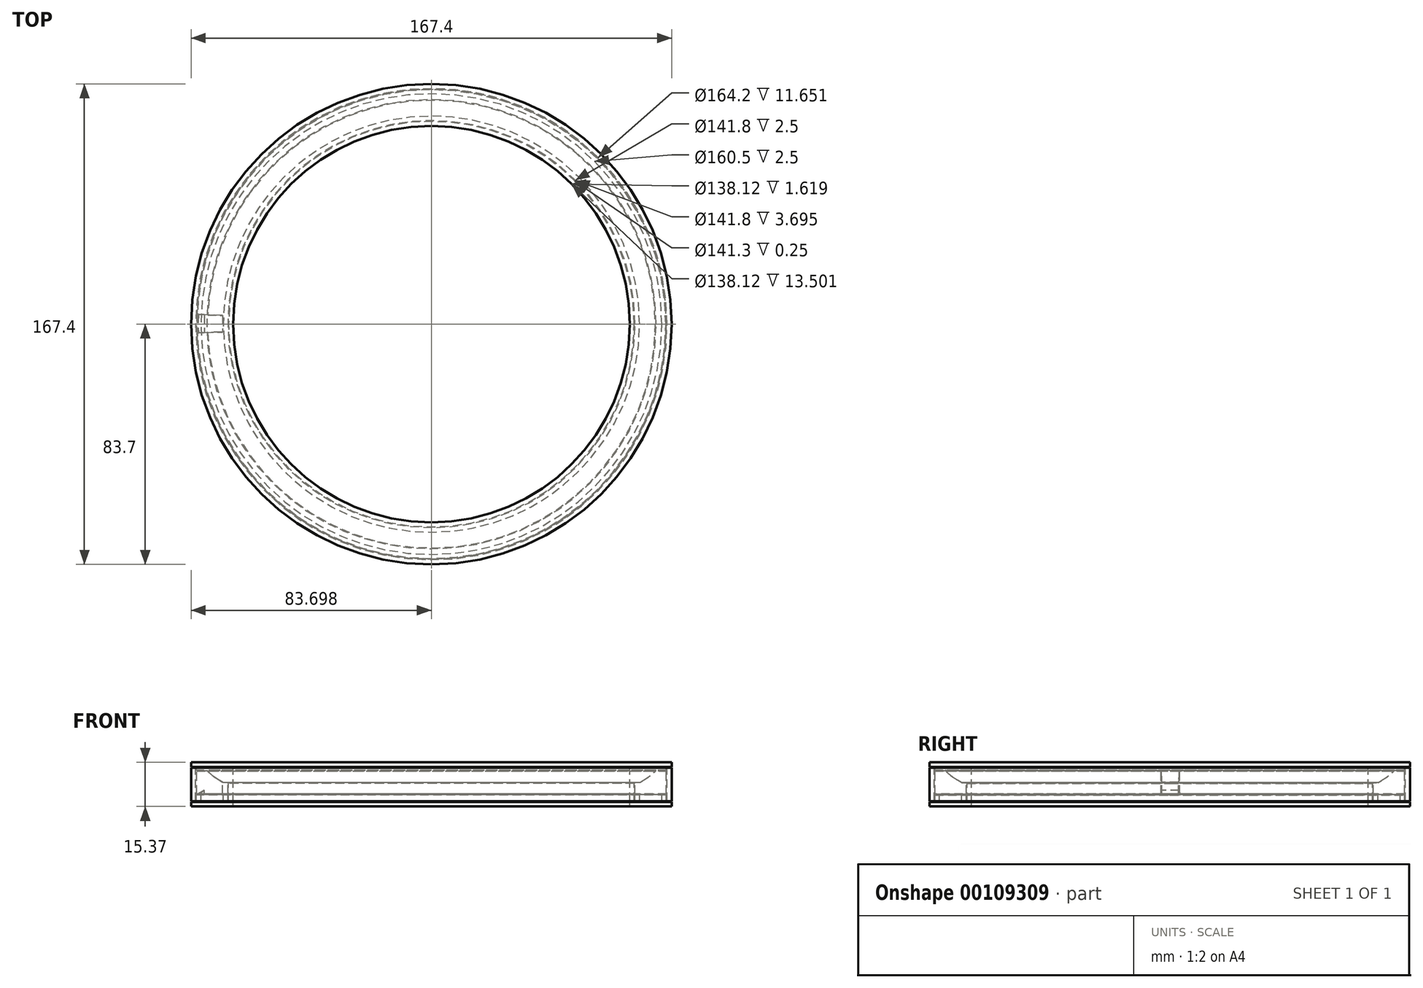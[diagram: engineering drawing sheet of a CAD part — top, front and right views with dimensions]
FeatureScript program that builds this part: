
annotation { "Feature Type Name" : "Feature", "Feature Type Description" : "" }
export const myFeature = defineFeature(function(context is Context, id is Id, definition is map)
    precondition{}
    {
        {
            var Q0;
            Q0=qCreatedBy(makeId("Front.planeOp"),FACE);
            var sketch = newSketch(context, id + "F0", { "sketchPlane" : qUnion([Q0])});
            skLineSegment(sketch, "E0", {"start": v(49.07, 29.5) * mm, "end": v(49.07, -21.25) * mm, "construction": true});
            skLineSegment(sketch, "E1", {"start": v(-23.43, 29.5) * mm, "end": v(-23.43, -21.25) * mm, "construction": true});
            skLineSegment(sketch, "E2", {"start": v(-30.18, 1.62) * mm, "end": v(-23.68, 1.62) * mm, "construction": true});
            skLineSegment(sketch, "E3", {"start": v(-23.68, 1.62) * mm, "end": v(-23.68, 4.12) * mm, "construction": true});
            skLineSegment(sketch, "E4", {"start": v(-23.68, 4.12) * mm, "end": v(-30.18, 4.12) * mm, "construction": true});
            skLineSegment(sketch, "E5", {"start": v(-30.18, 4.12) * mm, "end": v(-30.18, 1.62) * mm, "construction": true});
            skLineSegment(sketch, "E6", {"start": v(-29.18, 4.12) * mm, "end": v(-29.18, 4.92) * mm, "construction": true});
            skLineSegment(sketch, "E7", {"start": v(-29.18, 4.92) * mm, "end": v(-24.68, 4.92) * mm, "construction": true});
            skLineSegment(sketch, "E8", {"start": v(-24.68, 4.92) * mm, "end": v(-24.68, 4.12) * mm, "construction": true});
            skLineSegment(sketch, "E9", {"start": v(-35.93, 29.5) * mm, "end": v(-35.93, -21.25) * mm, "construction": true});
            skLineSegment(sketch, "E10", {"start": v(-31.18, 1.62) * mm, "end": v(-23.43, 1.62) * mm});
            skLineSegment(sketch, "E11", {"start": v(-31.18, 1.62) * mm, "end": v(-31.18, 4.12) * mm});
            skLineSegment(sketch, "E12", {"start": v(-34.74, 0.02) * mm, "end": v(-21.83, 0.02) * mm});
            skLineSegment(sketch, "E13", {"start": v(-23.43, 1.62) * mm, "end": v(-23.43, 3.24) * mm});
            skLineSegment(sketch, "E14", {"start": v(-23.43, 4.12) * mm, "end": v(-21.83, 4.12) * mm});
            skLineSegment(sketch, "E15", {"start": v(-21.83, 4.12) * mm, "end": v(-21.83, 0.02) * mm});
            skLineSegment(sketch, "E16", {"start": v(-24.68, 4.92) * mm, "end": v(-24.68, 12.8) * mm, "construction": true});
            skLineSegment(sketch, "E17", {"start": v(-29.18, 4.92) * mm, "end": v(-29.18, 12.8) * mm, "construction": true});
            skLineSegment(sketch, "E18", {"start": v(-82.01, -1.66) * mm, "end": v(-82.01, 10.37) * mm, "construction": true});
            skLineSegment(sketch, "E19", {"start": v(-23.43, 4.12) * mm, "end": v(-23.43, 1.62) * mm});
            skLineSegment(sketch, "E20", {"start": v(-72.42, 0.02) * mm, "end": v(839.7, 0.02) * mm, "construction": true});
            skLineSegment(sketch, "E21", {"start": v(-21.58, 1.87) * mm, "end": v(-21.58, 20.5) * mm});
            skLineSegment(sketch, "E22", {"start": v(-20, 1.87) * mm, "end": v(-20, 15.37) * mm});
            skLineSegment(sketch, "E23", {"start": v(-20, 15.37) * mm, "end": v(-34.63, 15.37) * mm});
            skLineSegment(sketch, "E24", {"start": v(-34.63, 13.52) * mm, "end": v(-33.03, 13.52) * mm});
            skLineSegment(sketch, "E25", {"start": v(-33.03, 13.52) * mm, "end": v(-33.03, 1.87) * mm});
            skLineSegment(sketch, "E26", {"start": v(-33.03, 1.87) * mm, "end": v(-34.63, 1.87) * mm});
            skLineSegment(sketch, "E27", {"start": v(-34.63, 1.87) * mm, "end": v(-34.63, 13.52) * mm});
            skLineSegment(sketch, "E28", {"start": v(-34.63, 0.02) * mm, "end": v(-34.74, 0.02) * mm});
            skLineSegment(sketch, "E29", {"start": v(-34.63, 0.02) * mm, "end": v(-34.63, 1.62) * mm});
            skLineSegment(sketch, "E30", {"start": v(-34.63, 1.62) * mm, "end": v(-32.78, 1.62) * mm});
            skLineSegment(sketch, "E31", {"start": v(-34.63, 15.37) * mm, "end": v(-34.63, 13.77) * mm});
            skLineSegment(sketch, "E32", {"start": v(-34.63, 13.77) * mm, "end": v(-32.78, 13.77) * mm});
            skLineSegment(sketch, "E33", {"start": v(-36.84, 4.37) * mm, "end": v(-22.3, 4.37) * mm, "construction": true});
            skLineSegment(sketch, "E34", {"start": v(-32.78, 1.62) * mm, "end": v(-32.78, 2.82) * mm});
            skLineSegment(sketch, "E35", {"start": v(-32.78, 13.77) * mm, "end": v(-32.78, 12.57) * mm});
            skLineSegment(sketch, "E36", {"start": v(-32.78, 12.57) * mm, "end": v(-28.4, 12.57) * mm});
            skLineSegment(sketch, "E37", {"start": v(-23.43, 8.31) * mm, "end": v(-21.58, 8.31) * mm});
            skLineSegment(sketch, "E38", {"start": v(-21.83, 4.37) * mm, "end": v(-31.4, 4.37) * mm});
            skLineSegment(sketch, "E39", {"start": v(-31.4, 4.37) * mm, "end": v(-32.78, 4.37) * mm});
            skLineSegment(sketch, "E40.0", {"start": v(-32.78, 12.32) * mm, "end": v(-28.4, 12.32) * mm});
            skLineSegment(sketch, "E41", {"start": v(-32.78, 12.32) * mm, "end": v(-32.78, 4.37) * mm});
            skLineSegment(sketch, "E42", {"start": v(-23.43, 8.31) * mm, "end": v(-24.68, 9.04) * mm});
            skLineSegment(sketch, "E43", {"start": v(-22.53, 10.28) * mm, "end": v(-40.3, 0.02) * mm, "construction": true});
            skArc(sketch, "E44", {"start": v(-24.68, 9.04) * mm, "mid": v(-27.06, 10.64) * mm, "end": v(-29.18, 12.57) * mm});
            skLineSegment(sketch, "E45", {"start": v(-29.18, 12.57) * mm, "end": v(-28.4, 12.57) * mm});
            skArc(sketch, "E46.0", {"start": v(-24.78, 8.8) * mm, "mid": v(-27.19, 10.43) * mm, "end": v(-29.34, 12.37) * mm});
            skLineSegment(sketch, "E47", {"start": v(-29.29, 12.32) * mm, "end": v(-28.4, 12.32) * mm});
            skLineSegment(sketch, "E48.0", {"start": v(-23.5, 8.06) * mm, "end": v(-24.8, 8.81) * mm});
            skLineSegment(sketch, "E49.0", {"start": v(-23.5, 8.06) * mm, "end": v(-21.56, 8.06) * mm});
            skLineSegment(sketch, "E50", {"start": v(-21.83, 4.37) * mm, "end": v(-21.83, 8.06) * mm});
            skLineSegment(sketch, "E51", {"start": v(-23.43, 4.37) * mm, "end": v(-23.43, 8.06) * mm});
            skLineSegment(sketch, "E52", {"start": v(-32.78, 4) * mm, "end": v(-32.58, 4.12) * mm});
            skLineSegment(sketch, "E53", {"start": v(-32.78, 2.82) * mm, "end": v(-32.78, 4) * mm});
            skLineSegment(sketch, "E54", {"start": v(-31.18, 4.12) * mm, "end": v(-32.58, 4.12) * mm});
            skLineSegment(sketch, "E55", {"start": v(-32.78, 4) * mm, "end": v(-30.18, 5.5) * mm, "construction": true});
            skLineSegment(sketch, "E56", {"start": v(-30.05, 5.58) * mm, "end": v(-32.14, 4.37) * mm});
            skLineSegment(sketch, "E57", {"start": v(-30.05, 5.58) * mm, "end": v(-30.05, 4.37) * mm});
            skLineSegment(sketch, "E58", {"start": v(-30.05, 4.37) * mm, "end": v(-32.14, 4.37) * mm});
            skLineSegment(sketch, "E59", {"start": v(-21.58, 1.87) * mm, "end": v(-20, 1.87) * mm});
            skLineSegment(sketch, "E60", {"start": v(-21.83, 1.62) * mm, "end": v(-20, 1.62) * mm});
            skLineSegment(sketch, "E61", {"start": v(-20, 1.62) * mm, "end": v(-20, 0) * mm});
            skLineSegment(sketch, "E62", {"start": v(-20, 0) * mm, "end": v(-21.83, 0.02) * mm});
            skSolve(sketch);
        }
        {
            var Q0;
            Q0=makeQuery(id+"F0.imprint","IMPRINT",FACE,{"disambiguationData":[TD([[makeQuery(id+"F0.imprint","IMPRINT",EDGE,{"derivedFrom":sQuery(id+"F0.wireOp",EDGE,"E40.0")}),-1.0]])]});
            var Q1;
            {var subQ0=sQuery(id+"F0.wireOp",EDGE,"E50");Q1=makeQuery(id+"F0.imprint","IMPRINT",FACE,{"disambiguationData":[TD([[makeQuery(id+"F0.imprint","IMPRINT",EDGE,{"derivedFrom":subQ0}),1.0]])]});}
            var Q2;
            {var subQ3=sQuery(id+"F0.wireOp",EDGE,"nZakiuLn-CLJS-k8i2-04lO-UVL3UxqrP7IB");Q2=makeQuery(id+"F0.imprint","IMPRINT",FACE,{"disambiguationData":[TD([[makeQuery(id+"F0.imprint","IMPRINT",EDGE,{"derivedFrom":subQ3}),1.0]])]});}
            var Q3;
            {var subQ0=sQuery(id+"F0.wireOp",EDGE,"E56");Q3=makeQuery(id+"F0.imprint","IMPRINT",FACE,{"disambiguationData":[TD([[makeQuery(id+"F0.imprint","IMPRINT",EDGE,{"derivedFrom":subQ0}),1.0]])]});}
            var Q4;
            Q4=sQuery(id+"F0.wireOp",EDGE,"E0");
            revolve(context, id + "F1", {"entities" : qUnion([Q0, Q1, Q2, Q3]), "axis" : qUnion([Q4]), "revolveType" : RevolveType.FULL});
        }
        {
            var Q0;
            Q0=makeQuery(id+"F1.opRevolve","SWEPT_FACE",FACE,{"disambiguationData":[OSD([sQuery(id+"F0.wireOp",EDGE,"E40.0"),sQuery(id+"F0.wireOp",EDGE,"E47")])]});
            var sketch = newSketch(context, id + "F2", { "sketchPlane" : qUnion([Q0])});
            skPoint(sketch, "E63.0", {"position": v(-30.18, 0) * mm});
            skPoint(sketch, "E64.0", {"position": v(-23.68, 0) * mm});
            skLineSegment(sketch, "E65.bottom", {"start": v(-23.68, -2.74) * mm, "end": v(-36.08, -3.2) * mm});
            skLineSegment(sketch, "E66", {"start": v(-36.07, 3.54) * mm, "end": v(49.07, 0) * mm, "construction": true});
            skLineSegment(sketch, "E67", {"start": v(49.07, 0) * mm, "end": v(-36.08, -3.2) * mm, "construction": true});
            skLineSegment(sketch, "E68", {"start": v(-34.44, 3.47) * mm, "end": v(-20.06, 2.87) * mm});
            skLineSegment(sketch, "E69", {"start": v(-20.06, -2.6) * mm, "end": v(-34.44, -3.14) * mm});
            skLineSegment(sketch, "E70", {"start": v(-34.44, -3.14) * mm, "end": v(-34.44, 3.47) * mm});
            skArc(sketch, "E71", {"start": v(-23.68, 0) * mm, "mid": v(-23.67, 1.5) * mm, "end": v(-23.62, 3.02) * mm});
            skArc(sketch, "E72", {"start": v(-23.68, 0) * mm, "mid": v(-23.67, -1.37) * mm, "end": v(-23.63, -2.74) * mm});
            skSolve(sketch);
        }
        {
            var Q0;
            Q0 = qSketchRegion(id + "F2", true);
            var Q1;
            Q1=makeQuery(id+"F1.opRevolve","SWEPT_FACE",FACE,{"disambiguationData":[OSD([sQuery(id+"F0.wireOp",EDGE,"E38"),sQuery(id+"F0.wireOp",EDGE,"E39"),sQuery(id+"F0.wireOp",EDGE,"E58")])]});
            extrude(context, id + "F3", {"entities" : qUnion([Q0]), "operationType" : NewBodyOperationType.REMOVE, "endBound" : BoundingType.UP_TO_SURFACE, "oppositeDirection" : true, "endBoundEntityFace" : qUnion([Q1]), "depth" : 25 * mm});
        }
        {
            var Q0;
            {var subQ0=sQuery(id+"F0.wireOp",EDGE,"E56");Q0=makeQuery(id+"F0.imprint","IMPRINT",FACE,{"disambiguationData":[TD([[makeQuery(id+"F0.imprint","IMPRINT",EDGE,{"derivedFrom":subQ0}),1.0]])]});}
            var Q1;
            Q1=sQuery(id+"F0.wireOp",EDGE,"E0");
            revolve(context, id + "F4", {"operationType" : NewBodyOperationType.ADD, "entities" : qUnion([Q0]), "axis" : qUnion([Q1]), "revolveType" : RevolveType.FULL});
        }
        {
            var Q0;
            {var subQ2=sQuery(id+"F0.wireOp",EDGE,"E60");Q0=makeQuery(id+"F0.imprint","IMPRINT",FACE,{"disambiguationData":[TD([[makeQuery(id+"F0.imprint","IMPRINT",EDGE,{"derivedFrom":subQ2}),-1.0]])]});}
            var Q1;
            {var subQ2=sQuery(id+"F0.wireOp",EDGE,"E10");Q1=makeQuery(id+"F0.imprint","IMPRINT",FACE,{"disambiguationData":[TD([[makeQuery(id+"F0.imprint","IMPRINT",EDGE,{"derivedFrom":subQ2}),-1.0]])]});}
            var Q2;
            Q2=sQuery(id+"F0.wireOp",EDGE,"E0");
            revolve(context, id + "F5", {"entities" : qUnion([Q0, Q1]), "axis" : qUnion([Q2]), "revolveType" : RevolveType.FULL});
        }
        {
            var Q0;
            {var subQ4=sQuery(id+"F0.wireOp",EDGE,"E31");Q0=makeQuery(id+"F0.imprint","IMPRINT",FACE,{"disambiguationData":[TD([[makeQuery(id+"F0.imprint","IMPRINT",EDGE,{"derivedFrom":subQ4}),1.0]])]});}
            var Q1;
            {var subQ0=sQuery(id+"F0.wireOp",EDGE,"u2Rdq3c2-eWa1-kzH8-av5P-0K82xw47kb6N");Q1=makeQuery(id+"F0.imprint","IMPRINT",FACE,{"disambiguationData":[TD([[makeQuery(id+"F0.imprint","IMPRINT",EDGE,{"derivedFrom":subQ0}),1.0]])]});}
            var Q2;
            {var subQ0=sQuery(id+"F0.wireOp",EDGE,"E22");Q2=makeQuery(id+"F0.imprint","IMPRINT",FACE,{"disambiguationData":[TD([[makeQuery(id+"F0.imprint","IMPRINT",EDGE,{"derivedFrom":subQ0}),1.0]])]});}
            var Q3;
            Q3=sQuery(id+"F0.wireOp",EDGE,"E0");
            revolve(context, id + "F6", {"entities" : qUnion([Q0, Q1, Q2]), "axis" : qUnion([Q3]), "revolveType" : RevolveType.FULL});
        }
        {
            var Q0;
            Q0=makeQuery(id+"F0.imprint","IMPRINT",FACE,{"disambiguationData":[TD([[makeQuery(id+"F0.imprint","IMPRINT",EDGE,{"derivedFrom":sQuery(id+"F0.wireOp",EDGE,"E24")}),-1.0]])]});
            var Q1;
            Q1=sQuery(id+"F0.wireOp",EDGE,"E0");
            revolve(context, id + "F7", {"entities" : qUnion([Q0]), "axis" : qUnion([Q1]), "revolveType" : RevolveType.FULL});
        }
    });
